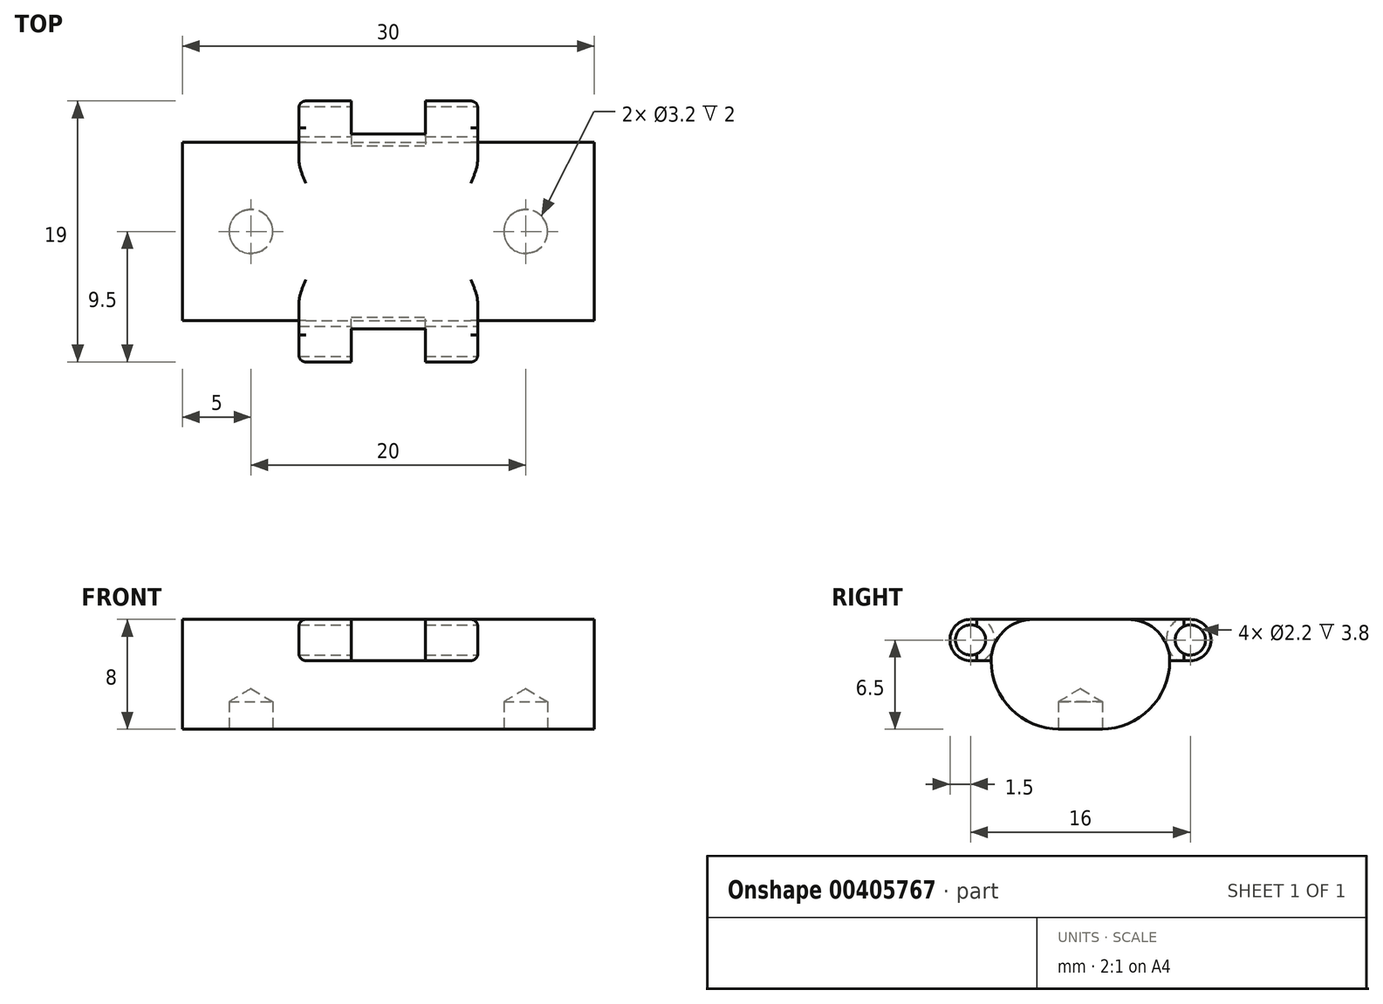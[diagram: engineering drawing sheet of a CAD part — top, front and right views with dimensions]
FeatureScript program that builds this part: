
annotation { "Feature Type Name" : "Feature", "Feature Type Description" : "" }
export const myFeature = defineFeature(function(context is Context, id is Id, definition is map)
    precondition{}
    {
        {
            var Q0;
            Q0=qCreatedBy(makeId("Top.planeOp"),FACE);
            var sketch = newSketch(context, id + "F0", { "sketchPlane" : qUnion([Q0])});
            skLineSegment(sketch, "E0.bottom", {"start": v(15, -6.5) * mm, "end": v(-15, -6.5) * mm});
            skLineSegment(sketch, "E0.top", {"start": v(15, 6.5) * mm, "end": v(-15, 6.5) * mm});
            skLineSegment(sketch, "E0.left", {"start": v(15, -6.5) * mm, "end": v(15, 6.5) * mm});
            skLineSegment(sketch, "E0.right", {"start": v(-15, -6.5) * mm, "end": v(-15, 6.5) * mm});
            skPoint(sketch, "E0.middle", {"position": v(0, 0) * mm});
            skSolve(sketch);
        }
        {
            var Q0;
            Q0=makeQuery(id+"F0.imprint","IMPRINT",FACE,{"disambiguationData":[TD([[makeQuery(id+"F0.imprint","IMPRINT",EDGE,{"derivedFrom":sQuery(id+"F0.wireOp",EDGE,"E0.bottom")}),-1.0]])]});
            extrude(context, id + "F1", {"entities" : qUnion([Q0]), "depth" : 4 * mm, "hasSecondDirection" : true, "secondDirectionOppositeDirection" : true, "secondDirectionDepth" : 4 * mm});
        }
        {
            var Q0;
            Q0=makeQuery(id+"F1.opExtrude","CAP_FACE",FACE,{"disambiguationData":[OSD([sQuery(id+"F0.wireOp",EDGE,"E0.bottom"),sQuery(id+"F0.wireOp",EDGE,"E0.top"),sQuery(id+"F0.wireOp",EDGE,"E0.left"),sQuery(id+"F0.wireOp",EDGE,"E0.right")])],"isStart":true});
            var sketch = newSketch(context, id + "F2", { "sketchPlane" : qUnion([Q0])});
            skLineSegment(sketch, "E1", {"start": v(0, 0) * mm, "end": v(-10, 0) * mm, "construction": true});
            skLineSegment(sketch, "E2", {"start": v(0, 0) * mm, "end": v(10, 0) * mm, "construction": true});
            skPoint(sketch, "E3", {"position": v(-10, 0) * mm});
            skPoint(sketch, "E4", {"position": v(10, 0) * mm});
            skSolve(sketch);
        }
        {
            var Q0;
            Q0=sQuery(id+"F2.wireOp",VERTEX,"E3");
            var Q1;
            Q1=sQuery(id+"F2.wireOp",VERTEX,"E4");
            var Q2;
            Q2=makeQuery(id+"F1.opExtrude","SWEPT_BODY",BODY,{"disambiguationData":[OSD([sQuery(id+"F0.wireOp",EDGE,"E0.bottom"),sQuery(id+"F0.wireOp",EDGE,"E0.top"),sQuery(id+"F0.wireOp",EDGE,"E0.left"),sQuery(id+"F0.wireOp",EDGE,"E0.right")])]});
            hole(context, id + "F3", {"style" : HoleStyle.SIMPLE, "endStyle" : HoleEndStyle.BLIND, "holeDiameter" : 3.2 * mm, "holeDepth" : 2 * mm, "isTappedThrough" : true, "tappedDepth" : 12 * mm, "tapClearance" : 3, "startFromSketch" : true, "locations" : qUnion([Q0, Q1]), "scope" : qUnion([Q2])});
        }
        {
            var Q0;
            Q0=makeQuery(id+"F1.opExtrude","SWEPT_FACE",FACE,{"disambiguationData":[OSD([sQuery(id+"F0.wireOp",EDGE,"E0.bottom")])]});
            var sketch = newSketch(context, id + "F4", { "sketchPlane" : qUnion([Q0])});
            skLineSegment(sketch, "E5.bottom", {"start": v(0, 0) * mm, "end": v(6.5, 0) * mm, "construction": true});
            skLineSegment(sketch, "E6", {"start": v(6.5, 0) * mm, "end": v(6.5, 1) * mm, "construction": true});
            skLineSegment(sketch, "E7.bottom", {"start": v(6.5, 1) * mm, "end": v(-6.5, 1) * mm});
            skLineSegment(sketch, "E7.top", {"start": v(6.5, 4) * mm, "end": v(-6.5, 4) * mm});
            skLineSegment(sketch, "E7.left", {"start": v(6.5, 1) * mm, "end": v(6.5, 4) * mm});
            skLineSegment(sketch, "E7.right", {"start": v(-6.5, 1) * mm, "end": v(-6.5, 4) * mm});
            skSolve(sketch);
        }
        {
            var Q0;
            Q0=makeQuery(id+"F4.imprint","IMPRINT",FACE,{"disambiguationData":[TD([[makeQuery(id+"F4.imprint","IMPRINT",EDGE,{"derivedFrom":sQuery(id+"F4.wireOp",EDGE,"E7.bottom")}),-1.0]])]});
            extrude(context, id + "F5", {"entities" : qUnion([Q0]), "operationType" : NewBodyOperationType.ADD, "depth" : 3 * mm, "hasSecondDirection" : true, "secondDirectionOppositeDirection" : true, "secondDirectionDepth" : 16 * mm});
        }
        {
            var Q0;
            Q0=makeQuery(id+"F5.opExtrude","CAP_EDGE",EDGE,{"disambiguationData":[OSD([sQuery(id+"F4.wireOp",EDGE,"E7.top")])],"isStart":false});
            var Q1;
            Q1=makeQuery(id+"F5.opExtrude","CAP_EDGE",EDGE,{"disambiguationData":[OSD([sQuery(id+"F4.wireOp",EDGE,"E7.bottom")])],"isStart":false});
            var Q2;
            Q2=makeQuery(id+"F5.opExtrude","CAP_EDGE",EDGE,{"disambiguationData":[OSD([sQuery(id+"F4.wireOp",EDGE,"E7.top")])],"isStart":true});
            var Q3;
            Q3=makeQuery(id+"F5.opExtrude","CAP_EDGE",EDGE,{"disambiguationData":[OSD([sQuery(id+"F4.wireOp",EDGE,"E7.bottom")])],"isStart":true});
            fillet(context, id + "F6", {"entities" : qUnion([Q0, Q1, Q2, Q3]), "radius" : 1.5 * mm, "tangentPropagation" : true, "allowEdgeOverflow" : false});
        }
        {
            var Q0;
            Q0=qCreatedBy(makeId("Right.planeOp"),FACE);
            var sketch = newSketch(context, id + "F7", { "sketchPlane" : qUnion([Q0])});
            skLineSegment(sketch, "E8", {"start": v(0, 0) * mm, "end": v(-8, 0) * mm, "construction": true});
            skLineSegment(sketch, "E9", {"start": v(-8, 2.5) * mm, "end": v(-8, 0) * mm, "construction": true});
            skCircle(sketch, "E10", {"center": v(-8, 2.5) * mm, "radius": 1.75 * mm});
            skLineSegment(sketch, "E11", {"start": v(-8, 2.5) * mm, "end": v(8, 2.5) * mm, "construction": true});
            skCircle(sketch, "E12", {"center": v(8, 2.5) * mm, "radius": 1.75 * mm});
            skSolve(sketch);
        }
        {
            var Q0;
            Q0=makeQuery(id+"F7.imprint","IMPRINT",FACE,{"disambiguationData":[TD([[makeQuery(id+"F7.imprint","IMPRINT",EDGE,{"derivedFrom":sQuery(id+"F7.wireOp",EDGE,"E12")}),1.0]])]});
            var Q1;
            Q1=makeQuery(id+"F7.imprint","IMPRINT",FACE,{"disambiguationData":[TD([[makeQuery(id+"F7.imprint","IMPRINT",EDGE,{"derivedFrom":sQuery(id+"F7.wireOp",EDGE,"E10")}),1.0]])]});
            var Q2;
            Q2=sQuery(id+"F7.wireOp",EDGE,"E8");
            var Q3;
            Q3=sQuery(id+"F7.wireOp",EDGE,"E9");
            var Q4;
            Q4=sQuery(id+"F7.wireOp",EDGE,"E10");
            var Q5;
            Q5=sQuery(id+"F7.wireOp",EDGE,"E12");
            extrude(context, id + "F8", {"entities" : qUnion([Q0, Q1]), "operationType" : NewBodyOperationType.REMOVE, "surfaceEntities" : qUnion([Q2, Q3, Q4, Q5]), "oppositeDirection" : true, "depth" : 2.7 * mm, "hasSecondDirection" : true, "secondDirectionOppositeDirection" : false, "secondDirectionDepth" : 2.7 * mm});
        }
        {
            var Q0;
            {var subQ0=sQuery(id+"F4.wireOp",EDGE,"E7.left");var subQ3=sQuery(id+"F0.wireOp",EDGE,"E0.top");Q0=makeQuery(id+"F5.boolean.opBoolean","SPLIT",FACE,{"disambiguationData":[TD([makeQuery(id+"F1.opExtrude","SWEPT_FACE",FACE,{"disambiguationData":[OSD([subQ3])]})])],"derivedFrom":makeQuery(id+"F5.opExtrude","SWEPT_FACE",FACE,{"disambiguationData":[OSD([subQ0])]})});}
            var sketch = newSketch(context, id + "F9", { "sketchPlane" : qUnion([Q0])});
            skLineSegment(sketch, "E13", {"start": v(0, 0) * mm, "end": v(8, 0) * mm, "construction": true});
            skLineSegment(sketch, "E14", {"start": v(8, 0) * mm, "end": v(8, 2.5) * mm, "construction": true});
            skCircle(sketch, "E15", {"center": v(8, 2.5) * mm, "radius": 1.1 * mm});
            skLineSegment(sketch, "E16", {"start": v(8, 2.5) * mm, "end": v(-8, 2.5) * mm, "construction": true});
            skCircle(sketch, "E17", {"center": v(-8, 2.5) * mm, "radius": 1.1 * mm});
            skSolve(sketch);
        }
        {
            var Q0;
            Q0=makeQuery(id+"F9.imprint","IMPRINT",FACE,{"disambiguationData":[TD([[makeQuery(id+"F9.imprint","IMPRINT",EDGE,{"derivedFrom":sQuery(id+"F9.wireOp",EDGE,"E17")}),1.0]])]});
            var Q1;
            Q1=makeQuery(id+"F9.imprint","IMPRINT",FACE,{"disambiguationData":[TD([[makeQuery(id+"F9.imprint","IMPRINT",EDGE,{"derivedFrom":sQuery(id+"F9.wireOp",EDGE,"E15")}),1.0]])]});
            extrude(context, id + "F10", {"entities" : qUnion([Q0, Q1]), "operationType" : NewBodyOperationType.REMOVE, "oppositeDirection" : true, "depth" : 25 * mm});
        }
        {
            var Q0;
            {var subQ0=sQuery(id+"F0.wireOp",EDGE,"E0.left");var subQ1=sQuery(id+"F0.wireOp",EDGE,"E0.top");Q0=makeQuery(id+"F5.boolean.opBoolean","SPLIT",EDGE,{"disambiguationData":[TD([makeQuery(id+"F1.opExtrude","SWEPT_FACE",FACE,{"disambiguationData":[OSD([subQ0])]})])],"derivedFrom":makeQuery(id+"F1.opExtrude","CAP_EDGE",EDGE,{"disambiguationData":[OSD([subQ1])],"isStart":false})});}
            var Q1;
            {var subQ0=sQuery(id+"F0.wireOp",EDGE,"E0.left");var subQ1=sQuery(id+"F0.wireOp",EDGE,"E0.bottom");Q1=makeQuery(id+"F5.boolean.opBoolean","SPLIT",EDGE,{"disambiguationData":[TD([makeQuery(id+"F1.opExtrude","SWEPT_FACE",FACE,{"disambiguationData":[OSD([subQ0])]})])],"derivedFrom":makeQuery(id+"F1.opExtrude","CAP_EDGE",EDGE,{"disambiguationData":[OSD([subQ1])],"isStart":false})});}
            var Q2;
            {var subQ0=sQuery(id+"F0.wireOp",EDGE,"E0.right");var subQ1=sQuery(id+"F0.wireOp",EDGE,"E0.bottom");Q2=makeQuery(id+"F5.boolean.opBoolean","SPLIT",EDGE,{"disambiguationData":[TD([makeQuery(id+"F1.opExtrude","SWEPT_FACE",FACE,{"disambiguationData":[OSD([subQ0])]})])],"derivedFrom":makeQuery(id+"F1.opExtrude","CAP_EDGE",EDGE,{"disambiguationData":[OSD([subQ1])],"isStart":false})});}
            var Q3;
            {var subQ0=sQuery(id+"F0.wireOp",EDGE,"E0.right");var subQ1=sQuery(id+"F0.wireOp",EDGE,"E0.top");Q3=makeQuery(id+"F5.boolean.opBoolean","SPLIT",EDGE,{"disambiguationData":[TD([makeQuery(id+"F1.opExtrude","SWEPT_FACE",FACE,{"disambiguationData":[OSD([subQ0])]})])],"derivedFrom":makeQuery(id+"F1.opExtrude","CAP_EDGE",EDGE,{"disambiguationData":[OSD([subQ1])],"isStart":false})});}
            fillet(context, id + "F11", {"entities" : qUnion([Q0, Q1, Q2, Q3]), "radius" : 3 * mm, "tangentPropagation" : true, "allowEdgeOverflow" : false});
        }
        {
            var Q0;
            Q0=makeQuery(id+"F1.opExtrude","CAP_EDGE",EDGE,{"disambiguationData":[OSD([sQuery(id+"F0.wireOp",EDGE,"E0.bottom")])],"isStart":true});
            var Q1;
            Q1=makeQuery(id+"F1.opExtrude","CAP_EDGE",EDGE,{"disambiguationData":[OSD([sQuery(id+"F0.wireOp",EDGE,"E0.top")])],"isStart":true});
            fillet(context, id + "F12", {"entities" : qUnion([Q0, Q1]), "radius" : 5 * mm, "tangentPropagation" : true, "allowEdgeOverflow" : false});
        }
        {
            var Q0;
            {var subQ0=sQuery(id+"F4.wireOp",EDGE,"E7.left");var subQ1=sQuery(id+"F4.wireOp",EDGE,"E7.top");var subQ2=sQuery(id+"F0.wireOp",EDGE,"E0.top");var subQ3=sQuery(id+"F0.wireOp",EDGE,"E0.bottom");Q0=makeQuery(id+"F5.boolean.opBoolean","SPLIT",EDGE,{"disambiguationData":[TD([makeQuery(id+"F1.opExtrude","SWEPT_FACE",FACE,{"disambiguationData":[OSD([subQ2])]})])],"derivedFrom":makeQuery(id+"F5.opExtrude","SWEPT_EDGE",EDGE,{"disambiguationData":[OSD([subQ3,subQ1,subQ0])]})});}
            var Q1;
            {var subQ0=sQuery(id+"F4.wireOp",EDGE,"E7.right");var subQ1=sQuery(id+"F4.wireOp",EDGE,"E7.top");var subQ2=sQuery(id+"F0.wireOp",EDGE,"E0.top");var subQ3=sQuery(id+"F0.wireOp",EDGE,"E0.bottom");Q1=makeQuery(id+"F5.boolean.opBoolean","SPLIT",EDGE,{"disambiguationData":[TD([makeQuery(id+"F1.opExtrude","SWEPT_FACE",FACE,{"disambiguationData":[OSD([subQ2])]})])],"derivedFrom":makeQuery(id+"F5.opExtrude","SWEPT_EDGE",EDGE,{"disambiguationData":[OSD([subQ3,subQ1,subQ0])]})});}
            var Q2;
            {var subQ0=sQuery(id+"F4.wireOp",EDGE,"E7.top");var subQ1=sQuery(id+"F4.wireOp",EDGE,"E7.left");var subQ2=sQuery(id+"F0.wireOp",EDGE,"E0.bottom");Q2=makeQuery(id+"F5.boolean.opBoolean","SPLIT",EDGE,{"disambiguationData":[TD([makeQuery(id+"F1.opExtrude","SWEPT_FACE",FACE,{"disambiguationData":[OSD([subQ2])]})])],"derivedFrom":makeQuery(id+"F5.opExtrude","SWEPT_EDGE",EDGE,{"disambiguationData":[OSD([subQ2,subQ0,subQ1])]})});}
            var Q3;
            {var subQ0=sQuery(id+"F4.wireOp",EDGE,"E7.top");var subQ1=sQuery(id+"F4.wireOp",EDGE,"E7.right");var subQ2=sQuery(id+"F0.wireOp",EDGE,"E0.bottom");Q3=makeQuery(id+"F5.boolean.opBoolean","SPLIT",EDGE,{"disambiguationData":[TD([makeQuery(id+"F1.opExtrude","SWEPT_FACE",FACE,{"disambiguationData":[OSD([subQ2])]})])],"derivedFrom":makeQuery(id+"F5.opExtrude","SWEPT_EDGE",EDGE,{"disambiguationData":[OSD([subQ2,subQ0,subQ1])]})});}
            fillet(context, id + "F13", {"entities" : qUnion([Q0, Q1, Q2, Q3]), "radius" : 0.5 * mm, "tangentPropagation" : true, "allowEdgeOverflow" : false});
        }
    });
